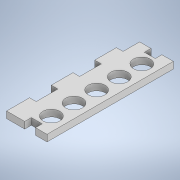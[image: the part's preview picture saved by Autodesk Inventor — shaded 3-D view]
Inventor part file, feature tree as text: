
AUTODESK INVENTOR PART (.ipt)
format: ipt  version: 2020 (Build 240168000, 168)  size: 150,528 bytes
history: native  units: mm
features: extrude x1, sketch x1
ambient origin geometry x8: Origin, YZ Plane, XZ Plane, XY Plane, X Axis, Y Axis, Z Axis, Center Point
bodies: Body1 (feature_tree)
feature tree (2):
  extrude  "Extrusion2"  Depth=112.0mm
  sketch  "Esquisse1"
